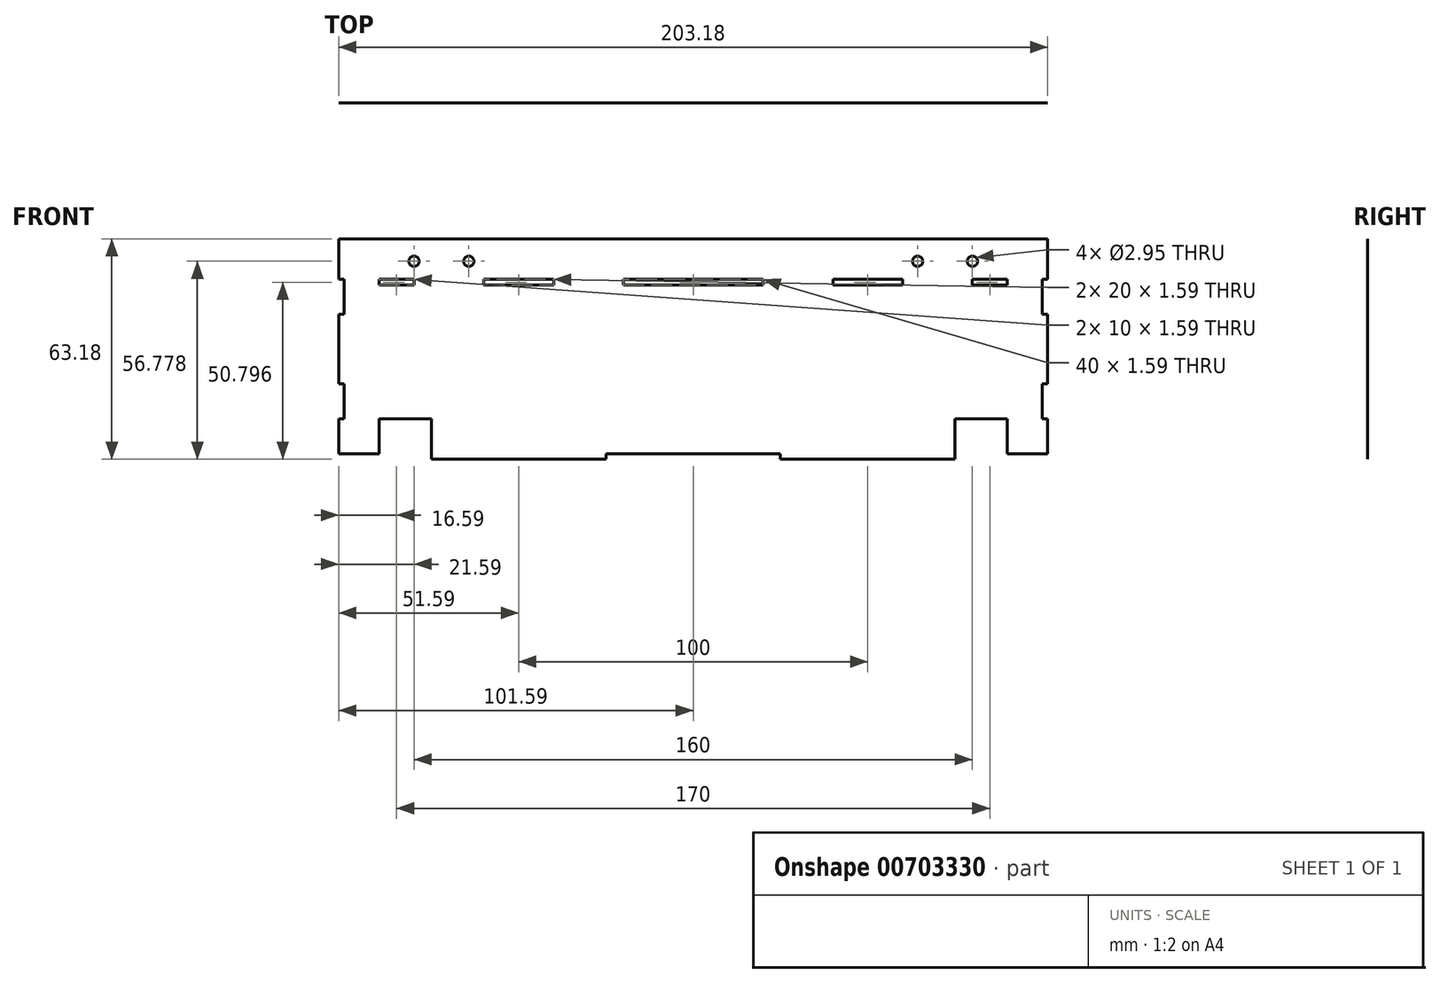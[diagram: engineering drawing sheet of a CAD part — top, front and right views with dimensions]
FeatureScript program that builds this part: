
annotation { "Feature Type Name" : "Feature", "Feature Type Description" : "" }
export const myFeature = defineFeature(function(context is Context, id is Id, definition is map)
    precondition{}
    {
        {
            var Q0;
            Q0=qCreatedBy(makeId("Front.planeOp"),FACE);
            var sketch = newSketch(context, id + "F0", { "sketchPlane" : qUnion([Q0])});
            skLineSegment(sketch, "E0.bottom", {"start": v(100, 30) * mm, "end": v(-100, 30) * mm});
            skLineSegment(sketch, "E0.top", {"start": v(100, -30) * mm, "end": v(-100, -30) * mm});
            skLineSegment(sketch, "E0.left", {"start": v(100, 30) * mm, "end": v(100, -30) * mm});
            skLineSegment(sketch, "E0.right", {"start": v(-100, 30) * mm, "end": v(-100, -30) * mm});
            skPoint(sketch, "E0.middle", {"position": v(0, 0) * mm});
            skLineSegment(sketch, "E1", {"start": v(-100, 10) * mm, "end": v(-101.59, 10) * mm});
            skLineSegment(sketch, "E2", {"start": v(-101.59, 10) * mm, "end": v(-101.59, -10) * mm});
            skLineSegment(sketch, "E3", {"start": v(-101.59, -10) * mm, "end": v(-100, -10) * mm});
            skLineSegment(sketch, "E4", {"start": v(100, 10) * mm, "end": v(101.59, 10) * mm});
            skLineSegment(sketch, "E5", {"start": v(101.59, 10) * mm, "end": v(101.59, -10) * mm});
            skLineSegment(sketch, "E6", {"start": v(101.59, -10) * mm, "end": v(100, -10) * mm});
            skLineSegment(sketch, "E7", {"start": v(-75, -30) * mm, "end": v(-75, -31.59) * mm});
            skLineSegment(sketch, "E8", {"start": v(-75, -31.59) * mm, "end": v(-25, -31.59) * mm});
            skLineSegment(sketch, "E9", {"start": v(-25, -31.59) * mm, "end": v(-25, -30) * mm});
            skLineSegment(sketch, "E10", {"start": v(25, -30) * mm, "end": v(25, -31.59) * mm});
            skLineSegment(sketch, "E11", {"start": v(25, -31.59) * mm, "end": v(75, -31.59) * mm});
            skLineSegment(sketch, "E12", {"start": v(75, -31.59) * mm, "end": v(75, -30) * mm});
            skLineSegment(sketch, "E13", {"start": v(-101.59, 30) * mm, "end": v(-100, 30) * mm});
            skLineSegment(sketch, "E14", {"start": v(-101.59, 20) * mm, "end": v(-100, 20) * mm});
            skLineSegment(sketch, "E15", {"start": v(-101.59, 20) * mm, "end": v(-101.59, 30) * mm});
            skLineSegment(sketch, "E16", {"start": v(-100, -30) * mm, "end": v(-101.59, -30) * mm});
            skPoint(sketch, "E16.endSnap0", {"position": v(-101.59, 25) * mm});
            skLineSegment(sketch, "E17", {"start": v(-101.59, -30) * mm, "end": v(-101.59, -20) * mm});
            skLineSegment(sketch, "E18", {"start": v(-101.59, -20) * mm, "end": v(-100, -20) * mm});
            skLineSegment(sketch, "E19", {"start": v(100, 30) * mm, "end": v(101.59, 30) * mm});
            skLineSegment(sketch, "E20", {"start": v(101.59, 30) * mm, "end": v(101.59, 20) * mm});
            skLineSegment(sketch, "E21", {"start": v(101.59, 20) * mm, "end": v(100, 20) * mm});
            skLineSegment(sketch, "E22", {"start": v(100, -30) * mm, "end": v(101.59, -30) * mm});
            skLineSegment(sketch, "E23", {"start": v(101.59, -30) * mm, "end": v(101.59, -20) * mm});
            skLineSegment(sketch, "E24", {"start": v(101.59, -20) * mm, "end": v(100, -20) * mm});
            skLineSegment(sketch, "E25", {"start": v(-101.59, 30) * mm, "end": v(-101.59, 31.59) * mm});
            skLineSegment(sketch, "E26", {"start": v(-101.59, 31.59) * mm, "end": v(101.59, 31.59) * mm});
            skLineSegment(sketch, "E27", {"start": v(101.59, 31.59) * mm, "end": v(101.59, 30) * mm});
            skCircle(sketch, "E28", {"center": v(-80, 25.19) * mm, "radius": 1.47 * mm});
            skCircle(sketch, "E29", {"center": v(-64.3, 25.19) * mm, "radius": 1.47 * mm});
            skCircle(sketch, "E30", {"center": v(80, 25.19) * mm, "radius": 1.47 * mm});
            skCircle(sketch, "E31", {"center": v(64.3, 25.19) * mm, "radius": 1.47 * mm});
            skLineSegment(sketch, "E32", {"start": v(-75, -30) * mm, "end": v(-75, -20) * mm});
            skLineSegment(sketch, "E33", {"start": v(-75, -20) * mm, "end": v(-90, -20) * mm});
            skLineSegment(sketch, "E34", {"start": v(-90, -20) * mm, "end": v(-90, -30) * mm});
            skLineSegment(sketch, "E35", {"start": v(75, -30) * mm, "end": v(75, -20) * mm});
            skLineSegment(sketch, "E36", {"start": v(75, -20) * mm, "end": v(90, -20) * mm});
            skLineSegment(sketch, "E37", {"start": v(90, -20) * mm, "end": v(90, -30) * mm});
            skLineSegment(sketch, "E38.bottom", {"start": v(90, 20) * mm, "end": v(80, 20) * mm});
            skLineSegment(sketch, "E38.top", {"start": v(90, 18.41) * mm, "end": v(80, 18.41) * mm});
            skLineSegment(sketch, "E38.left", {"start": v(90, 20) * mm, "end": v(90, 18.41) * mm});
            skLineSegment(sketch, "E38.right", {"start": v(80, 20) * mm, "end": v(80, 18.41) * mm});
            skPoint(sketch, "E38.middle", {"position": v(85, 19.2) * mm});
            skLineSegment(sketch, "E39.bottom", {"start": v(40, 20) * mm, "end": v(60, 20) * mm});
            skLineSegment(sketch, "E39.top", {"start": v(40, 18.41) * mm, "end": v(60, 18.41) * mm});
            skLineSegment(sketch, "E39.left", {"start": v(40, 20) * mm, "end": v(40, 18.41) * mm});
            skLineSegment(sketch, "E39.right", {"start": v(60, 20) * mm, "end": v(60, 18.41) * mm});
            skPoint(sketch, "E39.middle", {"position": v(50, 19.2) * mm});
            skLineSegment(sketch, "E40.bottom", {"start": v(20, 20) * mm, "end": v(-20, 20) * mm});
            skLineSegment(sketch, "E40.top", {"start": v(20, 18.41) * mm, "end": v(-20, 18.41) * mm});
            skLineSegment(sketch, "E40.left", {"start": v(20, 20) * mm, "end": v(20, 18.41) * mm});
            skLineSegment(sketch, "E40.right", {"start": v(-20, 20) * mm, "end": v(-20, 18.41) * mm});
            skPoint(sketch, "E40.middle", {"position": v(0, 19.2) * mm});
            skLineSegment(sketch, "E41.bottom", {"start": v(-40, 20) * mm, "end": v(-60, 20) * mm});
            skLineSegment(sketch, "E41.top", {"start": v(-40, 18.41) * mm, "end": v(-60, 18.41) * mm});
            skLineSegment(sketch, "E41.left", {"start": v(-40, 20) * mm, "end": v(-40, 18.41) * mm});
            skLineSegment(sketch, "E41.right", {"start": v(-60, 20) * mm, "end": v(-60, 18.41) * mm});
            skPoint(sketch, "E41.middle", {"position": v(-50, 19.2) * mm});
            skLineSegment(sketch, "E42.bottom", {"start": v(-80, 20) * mm, "end": v(-90, 20) * mm});
            skLineSegment(sketch, "E42.top", {"start": v(-80, 18.41) * mm, "end": v(-90, 18.41) * mm});
            skLineSegment(sketch, "E42.left", {"start": v(-80, 20) * mm, "end": v(-80, 18.41) * mm});
            skLineSegment(sketch, "E42.right", {"start": v(-90, 20) * mm, "end": v(-90, 18.41) * mm});
            skPoint(sketch, "E42.middle", {"position": v(-85, 19.2) * mm});
            skSolve(sketch);
        }
        {
            var Q0;
            {var subQ0=sQuery(id+"F0.wireOp",EDGE,"E10");Q0=makeQuery(id+"F0.imprint","IMPRINT",FACE,{"disambiguationData":[TD([[makeQuery(id+"F0.imprint","IMPRINT",EDGE,{"derivedFrom":subQ0}),1.0]])]});}
            var Q1;
            {var subQ0=sQuery(id+"F0.wireOp",EDGE,"E7");Q1=makeQuery(id+"F0.imprint","IMPRINT",FACE,{"disambiguationData":[TD([[makeQuery(id+"F0.imprint","IMPRINT",EDGE,{"derivedFrom":subQ0}),1.0]])]});}
            var Q2;
            {var subQ0=sQuery(id+"F0.wireOp",EDGE,"E4");Q2=makeQuery(id+"F0.imprint","IMPRINT",FACE,{"disambiguationData":[TD([[makeQuery(id+"F0.imprint","IMPRINT",EDGE,{"derivedFrom":subQ0}),-1.0]])]});}
            var Q3;
            {var subQ0=sQuery(id+"F0.wireOp",EDGE,"E22");Q3=makeQuery(id+"F0.imprint","IMPRINT",FACE,{"disambiguationData":[TD([[makeQuery(id+"F0.imprint","IMPRINT",EDGE,{"derivedFrom":subQ0}),1.0]])]});}
            var Q4;
            {var subQ0=sQuery(id+"F0.wireOp",EDGE,"E1");Q4=makeQuery(id+"F0.imprint","IMPRINT",FACE,{"disambiguationData":[TD([[makeQuery(id+"F0.imprint","IMPRINT",EDGE,{"derivedFrom":subQ0}),1.0]])]});}
            var Q5;
            {var subQ0=sQuery(id+"F0.wireOp",EDGE,"E16");Q5=makeQuery(id+"F0.imprint","IMPRINT",FACE,{"disambiguationData":[TD([[makeQuery(id+"F0.imprint","IMPRINT",EDGE,{"derivedFrom":subQ0}),-1.0]])]});}
            var Q6;
            {var subQ0=sQuery(id+"F0.wireOp",EDGE,"E19");Q6=makeQuery(id+"F0.imprint","IMPRINT",FACE,{"disambiguationData":[TD([[makeQuery(id+"F0.imprint","IMPRINT",EDGE,{"derivedFrom":subQ0}),-1.0]])]});}
            var Q7;
            {var subQ0=sQuery(id+"F0.wireOp",EDGE,"E13");Q7=makeQuery(id+"F0.imprint","IMPRINT",FACE,{"disambiguationData":[TD([[makeQuery(id+"F0.imprint","IMPRINT",EDGE,{"derivedFrom":subQ0}),-1.0]])]});}
            var Q8;
            Q8=makeQuery(id+"F0.imprint","IMPRINT",FACE,{"disambiguationData":[TD([[makeQuery(id+"F0.imprint","IMPRINT",EDGE,{"derivedFrom":sQuery(id+"F0.wireOp",EDGE,"E0.bottom")}),-1.0]])]});
            var Q9;
            {var subQ10=sQuery(id+"F0.wireOp",EDGE,"E0.bottom");Q9=makeQuery(id+"F0.imprint","IMPRINT",FACE,{"disambiguationData":[TD([[makeQuery(id+"F0.imprint","IMPRINT",EDGE,{"derivedFrom":subQ10}),1.0]])]});}
            extrude(context, id + "F1", {"entities" : qUnion([Q0, Q1, Q2, Q3, Q4, Q5, Q6, Q7, Q8, Q9]), "depth" : 1 / 406.4 * mm, "offsetDistance" : 25 * mm});
        }
    });
